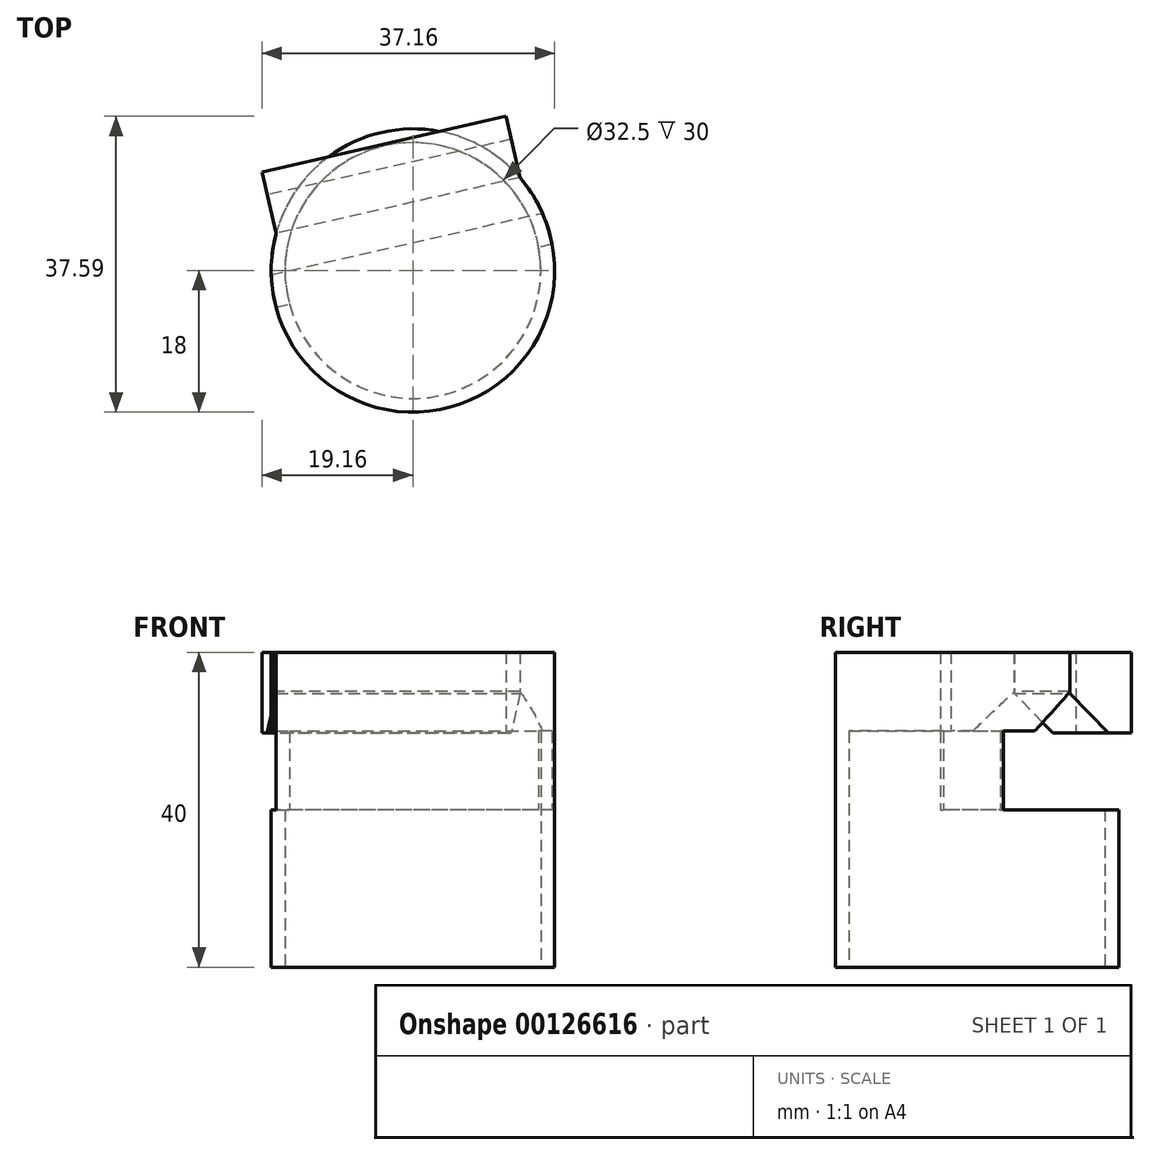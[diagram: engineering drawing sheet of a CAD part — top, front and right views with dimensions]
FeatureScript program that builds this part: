
annotation { "Feature Type Name" : "Feature", "Feature Type Description" : "" }
export const myFeature = defineFeature(function(context is Context, id is Id, definition is map)
    precondition{}
    {
        {
            var Q0;
            Q0=qCreatedBy(makeId("Top.planeOp"),FACE);
            var sketch = newSketch(context, id + "F0", { "sketchPlane" : qUnion([Q0])});
            skCircle(sketch, "E0", {"center": v(0, 0) * mm, "radius": 16.25 * mm});
            skCircle(sketch, "E1", {"center": v(0, 0) * mm, "radius": 18 * mm});
            skLineSegment(sketch, "E2", {"start": v(-17.39, -4.66) * mm, "end": v(-15.68, -4.27) * mm});
            skLineSegment(sketch, "E3", {"start": v(17.69, 3.34) * mm, "end": v(15.98, 2.95) * mm});
            skSolve(sketch);
        }
        {
            var Q0;
            {var subQ0=sQuery(id+"F0.wireOp",EDGE,"E2");Q0=makeQuery(id+"F0.imprint","IMPRINT",FACE,{"disambiguationData":[TD([[makeQuery(id+"F0.imprint","IMPRINT",EDGE,{"derivedFrom":subQ0}),-1.0]])]});}
            extrude(context, id + "F1", {"entities" : qUnion([Q0]), "depth" : 30 * mm});
        }
        {
            var Q0;
            Q0=qSketchRegion(id+"F0",true);
            extrude(context, id + "F2", {"entities" : qUnion([Q0]), "operationType" : NewBodyOperationType.ADD, "depth" : 20 * mm});
        }
        {
            var Q0;
            Q0=makeQuery(id+"F1.opExtrude","CAP_FACE",FACE,{"disambiguationData":[OSD([sQuery(id+"F0.wireOp",EDGE,"E0"),sQuery(id+"F0.wireOp",EDGE,"E1"),sQuery(id+"F0.wireOp",EDGE,"E2"),sQuery(id+"F0.wireOp",EDGE,"E3")])],"isStart":false});
            var sketch = newSketch(context, id + "F3", { "sketchPlane" : qUnion([Q0])});
            skLineSegment(sketch, "E4.0.0", {"start": v(-15.68, -4.27) * mm, "end": v(-17.39, -4.66) * mm});
            skArc(sketch, "E4.0.1", {"start": v(-17.39, -4.66) * mm, "mid": v(4, -17.55) * mm, "end": v(17.69, 3.34) * mm});
            skLineSegment(sketch, "E4.0.2", {"start": v(17.69, 3.34) * mm, "end": v(15.98, 2.95) * mm});
            skArc(sketch, "E4.0.3", {"start": v(15.98, 2.95) * mm, "mid": v(3.61, -15.84) * mm, "end": v(-15.68, -4.27) * mm});
            skLineSegment(sketch, "E5", {"start": v(-17.39, -4.66) * mm, "end": v(-17.39, -4.66) * mm});
            skLineSegment(sketch, "E6", {"start": v(-17.39, -4.66) * mm, "end": v(-15.68, -4.27) * mm});
            skLineSegment(sketch, "E7", {"start": v(17.69, 3.34) * mm, "end": v(17.69, 3.34) * mm});
            skLineSegment(sketch, "E8", {"start": v(-17.39, -4.66) * mm, "end": v(-17.69, -3.34) * mm});
            skLineSegment(sketch, "E9", {"start": v(-17.39, 4.73) * mm, "end": v(13.6, 11.8) * mm});
            skArc(sketch, "E10.0", {"start": v(17.69, 3.34) * mm, "mid": v(16.2, 7.84) * mm, "end": v(13.6, 11.8) * mm});
            skLineSegment(sketch, "E11", {"start": v(-17.39, 4.66) * mm, "end": v(-17.39, 4.73) * mm});
            skPoint(sketch, "E12.start.orphan", {"position": v(17.69, 12.73) * mm});
            skPoint(sketch, "E13.orphan", {"position": v(-17.39, -4.66) * mm});
            skArc(sketch, "E14.trimOffspring", {"start": v(-17.37, 4.74) * mm, "mid": v(-17.99, 0.72) * mm, "end": v(-17.69, -3.34) * mm});
            skLineSegment(sketch, "E15.trimOffspring", {"start": v(15.98, 2.95) * mm, "end": v(17.69, 3.34) * mm});
            skSolve(sketch);
        }
        {
            var Q0;
            Q0=qSketchRegion(id+"F3",true);
            extrude(context, id + "F4", {"entities" : qUnion([Q0]), "operationType" : NewBodyOperationType.ADD, "depth" : 10 * mm});
        }
        {
            var Q0;
            Q0=makeQuery(id+"F4.opExtrude","CAP_EDGE",EDGE,{"disambiguationData":[OSD([sQuery(id+"F3.wireOp",EDGE,"E9")])],"isStart":true});
            chamfer(context, id + "F5", {"entities" : qUnion([Q0]), "width" : 5 * mm, "tangentPropagation" : true});
        }
        {
            var Q0;
            Q0=makeQuery(id+"F4.opExtrude","SWEPT_FACE",FACE,{"disambiguationData":[OSD([sQuery(id+"F3.wireOp",EDGE,"E9")])]});
            var sketch = newSketch(context, id + "F6", { "sketchPlane" : qUnion([Q0])});
            skLineSegment(sketch, "E16.bottom", {"start": v(15.9, 40) * mm, "end": v(-15.88, 40) * mm});
            skLineSegment(sketch, "E16.top", {"start": v(15.9, 29.77) * mm, "end": v(-15.88, 29.77) * mm});
            skLineSegment(sketch, "E16.left", {"start": v(15.9, 40) * mm, "end": v(15.9, 29.77) * mm});
            skLineSegment(sketch, "E16.right", {"start": v(-15.88, 40) * mm, "end": v(-15.88, 29.77) * mm});
            skSolve(sketch);
        }
        {
            var Q0;
            Q0=qSketchRegion(id+"F6",true);
            var Q1;
            {var subQ0=sQuery(id+"F6.wireOp",EDGE,"E16.bottom");Q1=makeQuery(id+"F6.imprint","IMPRINT",FACE,{"disambiguationData":[TD([[makeQuery(id+"F6.imprint","IMPRINT",EDGE,{"derivedFrom":subQ0}),1.0]])]});}
            extrude(context, id + "F7", {"entities" : qUnion([Q0, Q1]), "operationType" : NewBodyOperationType.ADD, "depth" : 8 * mm});
        }
        {
            var Q0;
            Q0=makeQuery(id+"F7.opExtrude","CAP_EDGE",EDGE,{"disambiguationData":[OSD([sQuery(id+"F6.wireOp",EDGE,"E16.top")])],"isStart":true});
            chamfer(context, id + "F8", {"entities" : qUnion([Q0]), "width" : 5 * mm, "tangentPropagation" : true});
        }
    });
